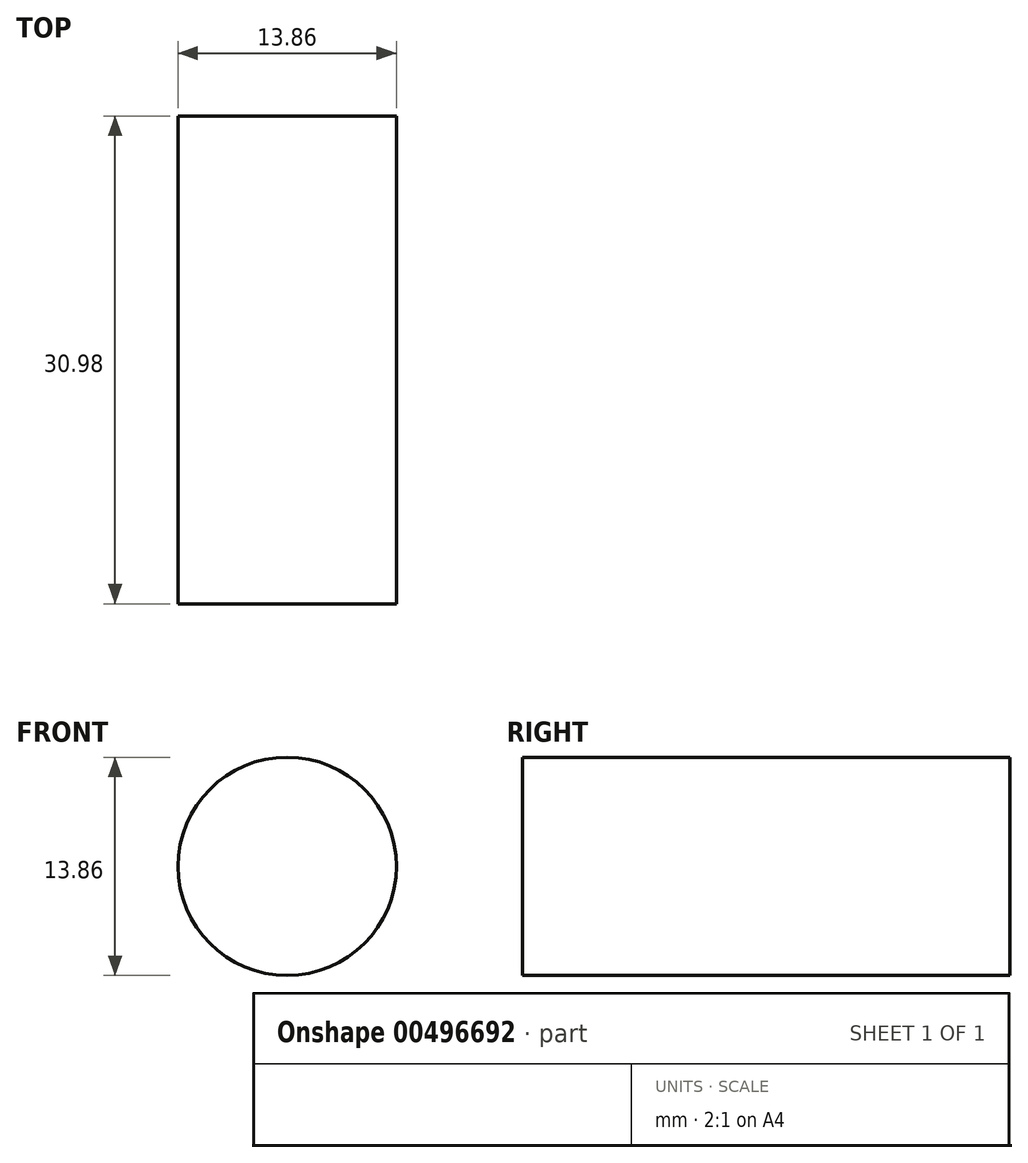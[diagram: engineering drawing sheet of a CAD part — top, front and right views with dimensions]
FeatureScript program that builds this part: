
annotation { "Feature Type Name" : "Feature", "Feature Type Description" : "" }
export const myFeature = defineFeature(function(context is Context, id is Id, definition is map)
    precondition{}
    {
        {
            var Q0;
            Q0=qCreatedBy(makeId("Front.planeOp"),FACE);
            var sketch = newSketch(context, id + "F0", { "sketchPlane" : qUnion([Q0])});
            skCircle(sketch, "E0", {"center": v(0, 0) * mm, "radius": 6.93 * mm});
            skSolve(sketch);
        }
        {
            var Q0;
            Q0=makeQuery(id+"F0.imprint","IMPRINT",FACE,{"disambiguationData":[TD([[makeQuery(id+"F0.imprint","IMPRINT",EDGE,{"derivedFrom":sQuery(id+"F0.wireOp",EDGE,"E0")}),1.0]])]});
            extrude(context, id + "F1", {"entities" : qUnion([Q0]), "endBound" : BoundingType.SYMMETRIC, "depth" : 30.99 * mm});
        }
    });
